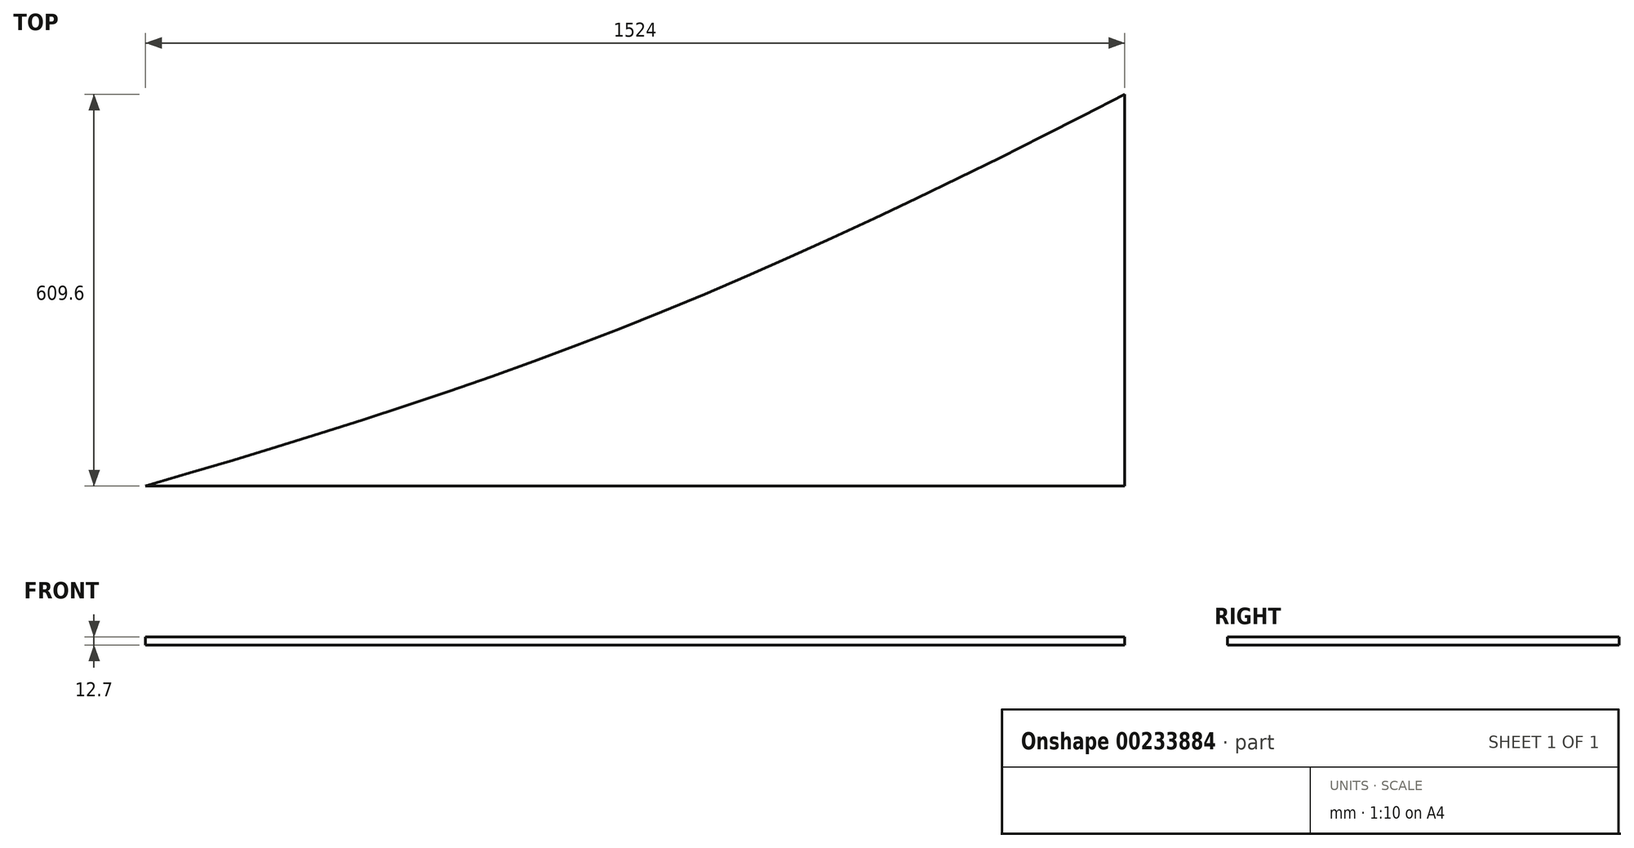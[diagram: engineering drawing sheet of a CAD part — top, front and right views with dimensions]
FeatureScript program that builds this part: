
annotation { "Feature Type Name" : "Feature", "Feature Type Description" : "" }
export const myFeature = defineFeature(function(context is Context, id is Id, definition is map)
    precondition{}
    {
        {
            var Q0;
            Q0=qCreatedBy(makeId("Top.planeOp"),FACE);
            var sketch = newSketch(context, id + "F0", { "sketchPlane" : qUnion([Q0])});
            skLineSegment(sketch, "E0", {"start": v(0, 609.6) * mm, "end": v(0, 0) * mm});
            skPoint(sketch, "E1", {"position": v(-1524, 0) * mm});
            skLineSegment(sketch, "E2", {"start": v(-1524, 0) * mm, "end": v(0, 0) * mm});
            skLineSegment(sketch, "E3", {"start": v(-762, 0) * mm, "end": v(-762, 254) * mm, "construction": true});
            skFitSpline(sketch, "E4", {"points": [v(-1524, 0) * mm, v(-762, 254) * mm, v(0, 609.6) * mm], "startDerivative": vector(1578.32, 457.71) * mm, "endDerivative": vector(1469.77, 761.24) * mm});
            skSolve(sketch);
        }
        {
            var Q0;
            Q0=makeQuery(id+"F0.imprint","IMPRINT",FACE,{"disambiguationData":[TD([[makeQuery(id+"F0.imprint","IMPRINT",EDGE,{"derivedFrom":sQuery(id+"F0.wireOp",EDGE,"E0")}),-1.0]])]});
            extrude(context, id + "F1", {"entities" : qUnion([Q0]), "depth" : 12.7 * mm});
        }
    });
